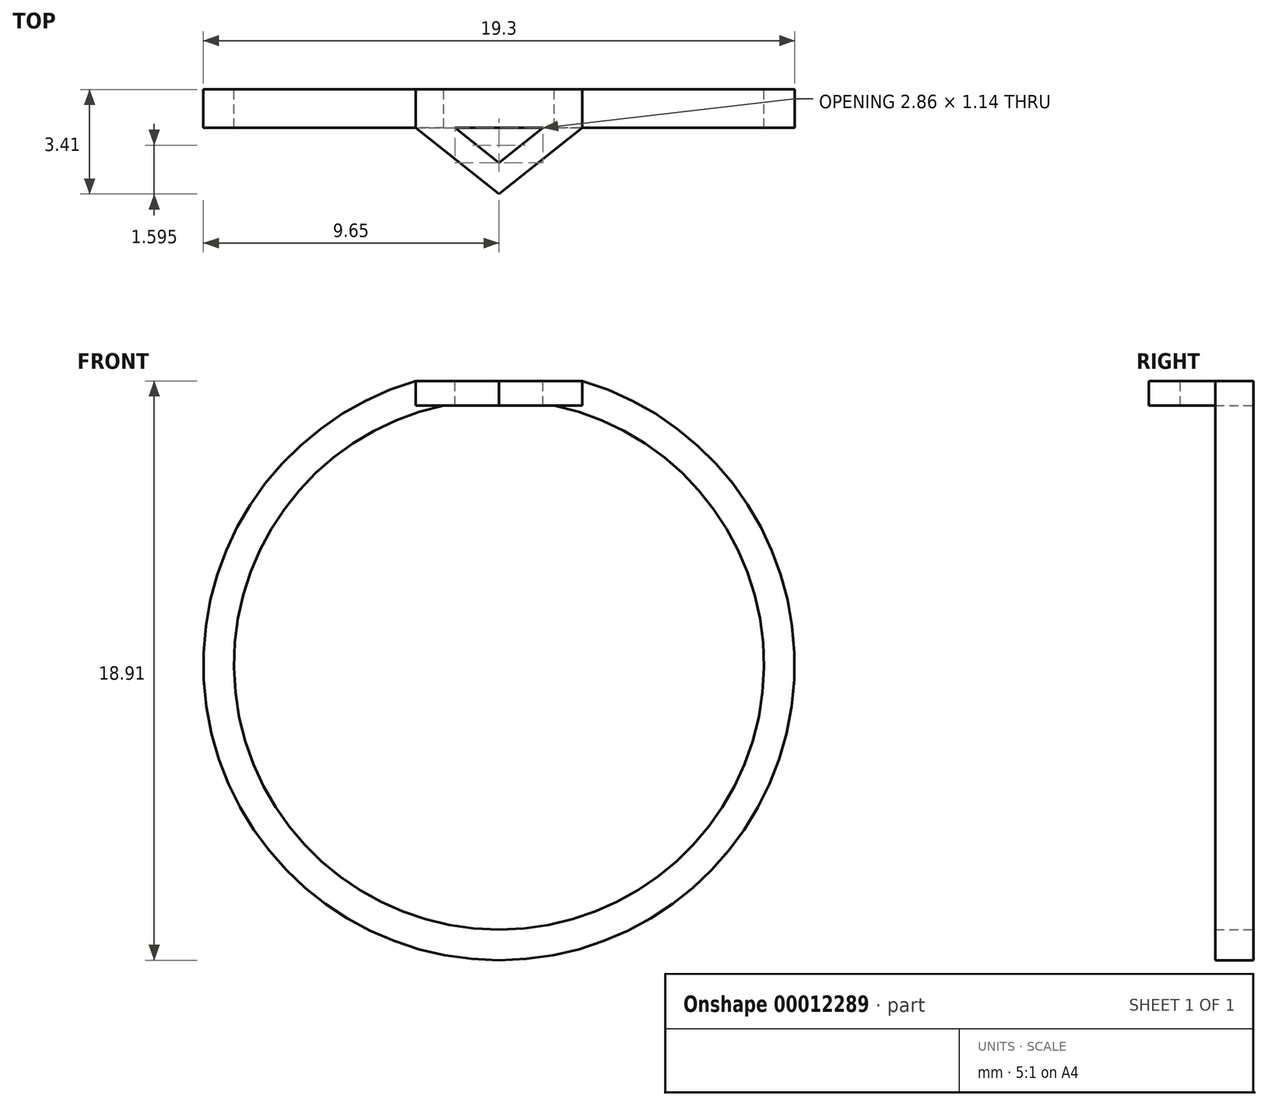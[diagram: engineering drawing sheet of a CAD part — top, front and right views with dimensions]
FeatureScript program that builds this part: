
annotation { "Feature Type Name" : "Feature", "Feature Type Description" : "" }
export const myFeature = defineFeature(function(context is Context, id is Id, definition is map)
    precondition{}
    {
        {
            var Q0;
            Q0=qCreatedBy(makeId("Front.planeOp"),FACE);
            var sketch = newSketch(context, id + "F0", { "sketchPlane" : qUnion([Q0])});
            skCircle(sketch, "E0", {"center": v(0, 0) * mm, "radius": 8.65 * mm});
            skCircle(sketch, "E1", {"center": v(0, 0) * mm, "radius": 9.65 * mm});
            skLineSegment(sketch, "E2", {"start": v(0, 0) * mm, "end": v(2.72, 9.26) * mm});
            skLineSegment(sketch, "E3", {"start": v(2.72, 9.26) * mm, "end": v(-2.72, 9.26) * mm});
            skLineSegment(sketch, "E4", {"start": v(-2.72, 9.26) * mm, "end": v(0, 0) * mm});
            skSolve(sketch);
        }
        {
            var Q0;
            {var subQ1=sQuery(id+"F0.wireOp",EDGE,"E0");var subQ6=sQuery(id+"F0.wireOp",EDGE,"5641d046-0c19-4be3-92f9-0dd0eed65a8e");var subQ7=makeQuery(id+"F0.imprint","INTERSECT",VERTEX,{"derivedFrom":[subQ1,subQ6]});Q0=makeQuery(id+"F0.imprint","IMPRINT",FACE,{"disambiguationData":[TD([[makeQuery(id+"F0.imprint","IMPRINT",EDGE,{"disambiguationData":[TD([[subQ7,1.0]])],"derivedFrom":subQ1}),-1.0]])]});}
            var Q1;
            {var subQ1=sQuery(id+"F0.wireOp",EDGE,"E0");var subQ3=sQuery(id+"F0.wireOp",EDGE,"ceee7dc4-5b8d-4878-b372-f6285a4e29ab");var subQ5=makeQuery(id+"F0.imprint","INTERSECT",VERTEX,{"derivedFrom":[subQ1,subQ3]});Q1=makeQuery(id+"F0.imprint","IMPRINT",FACE,{"disambiguationData":[TD([[makeQuery(id+"F0.imprint","IMPRINT",EDGE,{"disambiguationData":[TD([[subQ5,1.0]])],"derivedFrom":subQ1}),-1.0]])]});}
            var Q2;
            {var subQ1=sQuery(id+"F0.wireOp",EDGE,"E0");var subQ3=sQuery(id+"F0.wireOp",EDGE,"ceee7dc4-5b8d-4878-b372-f6285a4e29ab");var subQ5=makeQuery(id+"F0.imprint","INTERSECT",VERTEX,{"derivedFrom":[subQ1,subQ3]});Q2=makeQuery(id+"F0.imprint","IMPRINT",FACE,{"disambiguationData":[TD([[makeQuery(id+"F0.imprint","IMPRINT",EDGE,{"disambiguationData":[TD([[subQ5,-1.0]])],"derivedFrom":subQ1}),-1.0]])]});}
            extrude(context, id + "F1", {"entities" : qUnion([Q0, Q1, Q2]), "depth" : .625 * mm, "hasSecondDirection" : true, "secondDirectionOppositeDirection" : true, "secondDirectionDepth" : .625 * mm});
        }
        {
            var Q0;
            Q0=makeQuery(id+"F1.opExtrude","SWEPT_FACE",FACE,{"disambiguationData":[OSD([sQuery(id+"F0.wireOp",EDGE,"E3")])]});
            var sketch = newSketch(context, id + "F2", { "sketchPlane" : qUnion([Q0])});
            skLineSegment(sketch, "E5", {"start": v(2.72, 0.62) * mm, "end": v(-2.72, 0.62) * mm});
            skLineSegment(sketch, "E6", {"start": v(0, -1.77) * mm, "end": v(1.43, -0.62) * mm});
            skLineSegment(sketch, "E7", {"start": v(1.43, -0.62) * mm, "end": v(-1.43, -0.62) * mm});
            skLineSegment(sketch, "E8", {"start": v(-1.43, -0.62) * mm, "end": v(0, -1.77) * mm});
            skLineSegment(sketch, "E9", {"start": v(-2.72, -0.62) * mm, "end": v(0, -2.79) * mm});
            skLineSegment(sketch, "E10", {"start": v(0, -2.79) * mm, "end": v(2.72, -0.62) * mm});
            skSolve(sketch);
        }
        {
            var Q0;
            {var subQ7=sQuery(id+"F2.wireOp",EDGE,"E6");Q0=makeQuery(id+"F2.imprint","IMPRINT",FACE,{"disambiguationData":[TD([[makeQuery(id+"F2.imprint","IMPRINT",EDGE,{"derivedFrom":subQ7}),-1.0]])]});}
            var Q1;
            {var subQ8=sQuery(id+"F2.wireOp",EDGE,"E5");Q1=makeQuery(id+"F2.imprint","IMPRINT",FACE,{"disambiguationData":[TD([[makeQuery(id+"F2.imprint","IMPRINT",EDGE,{"derivedFrom":subQ8}),1.0]])]});}
            extrude(context, id + "F3", {"entities" : qUnion([Q0, Q1]), "operationType" : NewBodyOperationType.ADD, "oppositeDirection" : true, "depth" : .8 * mm});
        }
    });
